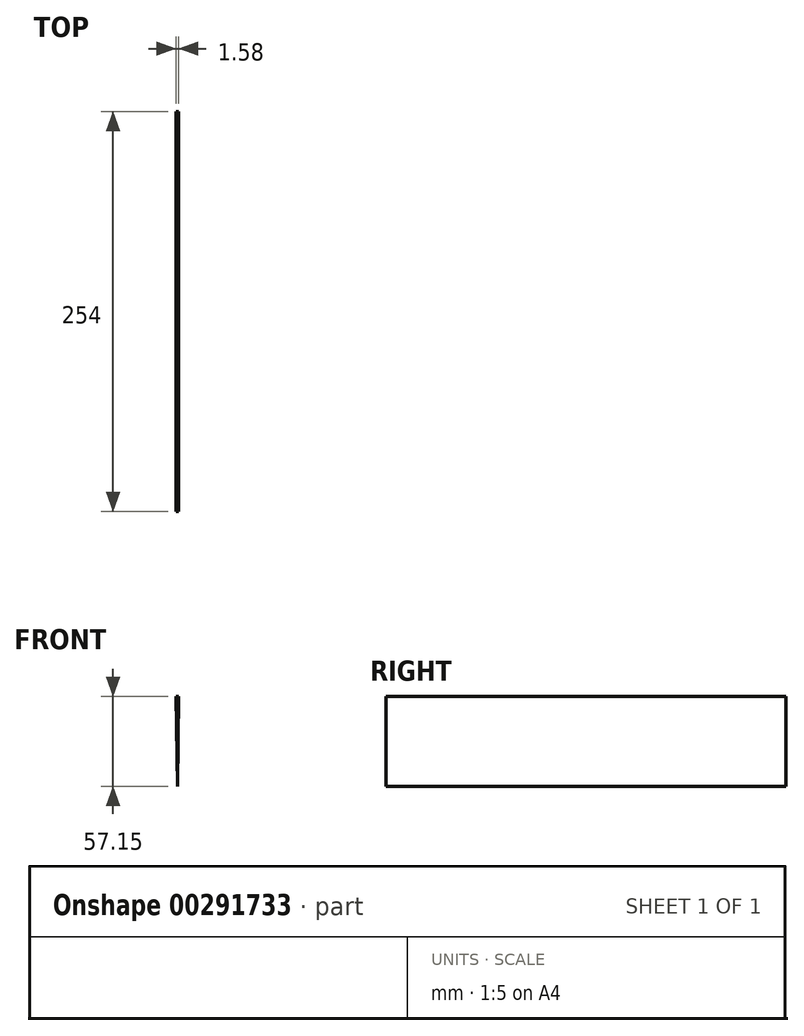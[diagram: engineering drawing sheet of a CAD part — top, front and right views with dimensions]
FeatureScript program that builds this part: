
annotation { "Feature Type Name" : "Feature", "Feature Type Description" : "" }
export const myFeature = defineFeature(function(context is Context, id is Id, definition is map)
    precondition{}
    {
        {
            var Q0;
            Q0=qCreatedBy(makeId("Front.planeOp"),FACE);
            var sketch = newSketch(context, id + "F0", { "sketchPlane" : qUnion([Q0])});
            skLineSegment(sketch, "E0", {"start": v(-0.8, 0) * mm, "end": v(0.8, 0) * mm});
            skPoint(sketch, "E1", {"position": v(0, -57.15) * mm});
            skLineSegment(sketch, "E2", {"start": v(-0.8, 0) * mm, "end": v(0, -57.15) * mm});
            skLineSegment(sketch, "E3", {"start": v(0.8, 0) * mm, "end": v(0, -57.15) * mm});
            skSolve(sketch);
        }
        {
            var Q0;
            Q0=qCreatedBy(makeId("Front.planeOp"),FACE);
            cPlane(context, id + "F1", {"entities" : qUnion([Q0]), "cplaneType" : CPlaneType.OFFSET, "offset" : 254 * mm, "oppositeDirection" : true, "width" : 152.4 * mm, "height" : 152.4 * mm});
        }
        {
            var Q0;
            Q0=qCreatedBy(id+"F1.planeOp",FACE);
            var sketch = newSketch(context, id + "F2", { "sketchPlane" : qUnion([Q0])});
            skPoint(sketch, "E4", {"position": v(0, 0) * mm});
            skSolve(sketch);
        }
        {
            var Q0;
            Q0=qCreatedBy(makeId("Right.planeOp"),FACE);
            var sketch = newSketch(context, id + "F3", { "sketchPlane" : qUnion([Q0])});
            skLineSegment(sketch, "E5", {"start": v(0, 0) * mm, "end": v(254, 0) * mm});
            skFitSpline(sketch, "E6", {"points": [v(254, 0) * mm, v(0, -57.15) * mm], "startDerivative": vector(-86.8, -146.3) * mm, "endDerivative": vector(-209.4, 10.04) * mm});
            skSolve(sketch);
        }
        {
            var Q0;
            Q0 = qSketchRegion(id + "F0", true);
            var Q1;
            Q1=sQuery(id+"F0.wireOp",EDGE,"E2");
            var Q2;
            Q2=sQuery(id+"F2.wireOp",VERTEX,"E4");
            extrude(context, id + "F4", {"entities" : qUnion([Q0]), "surfaceEntities" : qUnion([Q1]), "endBound" : BoundingType.UP_TO_VERTEX, "oppositeDirection" : true, "endBoundEntityVertex" : qUnion([Q2]), "depth" : 253.75 * mm});
        }
        {
            var Q0;
            Q0 = qSketchRegion(id + "F3", true);
            var Q1;
            Q1=makeQuery(id+"F4.opExtrude","SWEPT_FACE",FACE,{"disambiguationData":[OSD([sQuery(id+"F0.wireOp",EDGE,"E3")])]});
            var Q2;
            Q2=sQuery(id+"F3.wireOp",EDGE,"E6");
            extrude(context, id + "F5", {"entities" : qUnion([Q0, Q1]), "bodyType" : ToolBodyType.SURFACE, "operationType" : NewBodyOperationType.REMOVE, "surfaceEntities" : qUnion([Q2]), "endBound" : BoundingType.SYMMETRIC, "oppositeDirection" : true, "depth" : 25.4 * mm});
        }
    });
